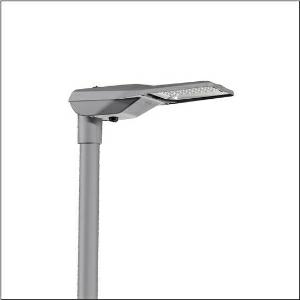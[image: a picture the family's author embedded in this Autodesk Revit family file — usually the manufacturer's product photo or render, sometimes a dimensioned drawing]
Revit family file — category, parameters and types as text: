
# Revit family: streetlight_sl_21_mini___st1_0a_5xe2d43t08gb_73de
name_source: partatom
category: Lighting Fixtures
units: mm (PartAtom-declared; Revit-internal decimal feet)

## family parameters
Cut with Voids When Loaded = No
Host = Face
Light Source = No
Part Type = Normal
Room Calculation Point = No
Round Connector Dimension = Use Diameter
Shared = No

## types (1)
- --- (1 x LED, 6180 lm, 40.4 W, 4000K)
    Apparent Load = 40 VA
    CIE Flux Codes = 37 72 97 100 100
    Color Rendering = 70
    Color Temperature = 4000K
    Default Elevation = 1800 mm
    Description = Streetlight SL 21 mini, mast luminaire, primary light control with lens, of PMMA, primary optical cover: cover, of toughened safety glass, transparent, light distribution: ST1.0a, light emission: direct distribution, primary light characteristic: asymmetric, installation type: side-entry, post-top, LED, High Power LED, rated luminous flux: 6.180lm, luminous efficacy: 153lm/W, light colour: 740, colour temperature: 4000K, control gear: D4i, control: overheat protection, constant luminous flux control, time-dependent luminous flux control, flexible luminous flux parameterisation, pre-setting: logarithmic dimming characteristic, mains connection: 220..240V, AC, 50/60Hz, start of lifetime: 40W, end of service life: 41W, reduction: 19W, luminaire housing, of diecast aluminium, powder-coated, SITECO metallic grey (DB 702S), corrosivity category C5 high according to DIN EN ISO 12944, please order mast flange separately, inclination adjustable: 0°, 5°, 10°, 15°, sealing non-destructively replaceable, multi-level sealing system, length: 628mm, width: 235mm, height: 110mm, mast flange for spigot size: 42mm (side-entry): 5XC10008XM4, 60/48mm (side-entry/post-top): 5XC10108XM2, 76/60mm (side-entry/post-top): 5XC10108XM1, mounting height: 4..8m, Smart Interface below and above, protection rating (complete): IP66, insulation class (complete): insulation class II (safety insulation), certification: CE, ENEC, ENEC+, VDE, impact resistance: IK10, permissible operating ambient temperature for outdoor applications: -40..+50°C, standard-compliant lighting for roads and squares, packaging unit: 1 piece

Light Distribution: ST1.0a
    Height = 110 mm
    Lamp = 1 x LED
    Lamp Light Flux = 6180 lm
    Lamp Power = 40.4 W
    Lamp count = 1
    Length = 625 mm
    Luminous efficacy = 153 lm/W
    Manufacturer = Siteco
    ModVariant = No
    Model = 5XE2D43T08GB
    Number of Poles = 1
    OnlyDefault = Yes
    Power Factor = 1
    Product Name = Streetlight SL 21 mini | ST1.0a
    Product group = mast luminaire | pylon top
    ProductGroupID = 6100
    Protection Class = Protection class II
    Protection Degree = IP 66
    RLX_Detail_Level = 1
    RLX_Emergency_Light_Flux = 0 lm
    RLX_Emergency_Type = 0
    RLX_Emergency_Type_DB = No
    RlxData = <blob elided: 26289 chars, md5=f0b233dc>
    Socket = socket
    Standby Power = 0 W
    System Light Flux = 6180 lm
    System Power = 40 W
    Type Comments = factory setting: luminous flux: 100 % | dim-lin: 254 | 812 mA
    Type Image = l_1003514.jpg
    URL = http://relux.com
    VarID = @adj_186007
    Voltage = 0 V
    Weight = 0.00 kg
    Width = 234 mm

## geometry (parser evidence)
native form markers: Blend x4, Sweep x10
no freeform markers — native parametric forms only
